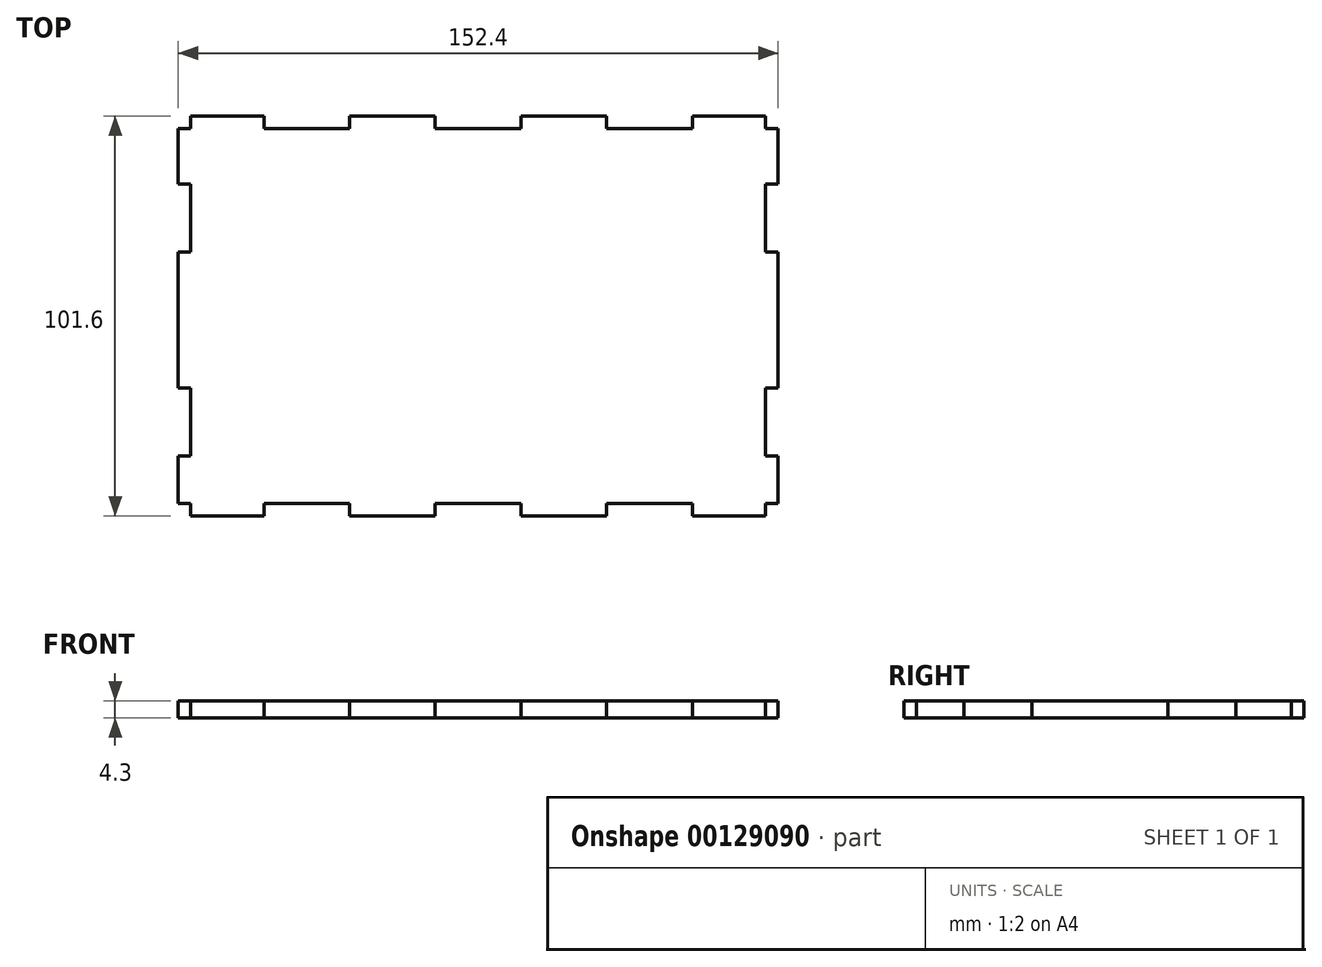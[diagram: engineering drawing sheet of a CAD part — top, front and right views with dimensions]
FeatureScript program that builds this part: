
annotation { "Feature Type Name" : "Feature", "Feature Type Description" : "" }
export const myFeature = defineFeature(function(context is Context, id is Id, definition is map)
    precondition{}
    {
        {
            var Q0;
            Q0=qCreatedBy(makeId("Top.planeOp"),FACE);
            var sketch = newSketch(context, id + "F0", { "sketchPlane" : qUnion([Q0])});
            skLineSegment(sketch, "E0.bottom", {"start": v(76.2, -50.8) * mm, "end": v(-76.2, -50.8) * mm});
            skLineSegment(sketch, "E0.top", {"start": v(76.2, 50.8) * mm, "end": v(-76.2, 50.8) * mm});
            skLineSegment(sketch, "E0.left", {"start": v(76.2, -50.8) * mm, "end": v(76.2, 50.8) * mm});
            skLineSegment(sketch, "E0.right", {"start": v(-76.2, -50.8) * mm, "end": v(-76.2, 50.8) * mm});
            skPoint(sketch, "E0.middle", {"position": v(0, 0) * mm});
            skLineSegment(sketch, "E1", {"start": v(-76.2, 50.8) * mm, "end": v(-73.03, 50.8) * mm});
            skLineSegment(sketch, "E2.0.1.0", {"start": v(-76.2, 33.53) * mm, "end": v(-73.03, 33.53) * mm});
            skLineSegment(sketch, "E2.0.2.0", {"start": v(-76.2, 16.27) * mm, "end": v(-73.03, 16.27) * mm});
            skLineSegment(sketch, "E2.0.3.0", {"start": v(-76.2, -1) * mm, "end": v(-73.03, -1) * mm});
            skLineSegment(sketch, "E2.0.4.0", {"start": v(-76.2, -18.27) * mm, "end": v(-73.03, -18.27) * mm});
            skLineSegment(sketch, "E2.0.5.0", {"start": v(-76.2, -35.53) * mm, "end": v(-73.03, -35.53) * mm});
            skLineSegment(sketch, "E2.direction1", {"start": v(-76.2, 50.8) * mm, "end": v(-50.8, 50.8) * mm, "construction": true});
            skLineSegment(sketch, "E2.direction2", {"start": v(-76.2, 50.8) * mm, "end": v(-76.2, 33.53) * mm, "construction": true});
            skLineSegment(sketch, "E3", {"start": v(-73.03, 50.8) * mm, "end": v(-73.02, -50.8) * mm});
            skLineSegment(sketch, "E4", {"start": v(-76.2, 50.8) * mm, "end": v(-76.2, 47.63) * mm});
            skLineSegment(sketch, "E5.1.0.0", {"start": v(-54.43, 50.8) * mm, "end": v(-54.43, 47.63) * mm});
            skLineSegment(sketch, "E5.2.0.0", {"start": v(-32.66, 50.8) * mm, "end": v(-32.66, 47.63) * mm});
            skLineSegment(sketch, "E5.3.0.0", {"start": v(-10.89, 50.8) * mm, "end": v(-10.89, 47.63) * mm});
            skLineSegment(sketch, "E5.4.0.0", {"start": v(10.89, 50.8) * mm, "end": v(10.89, 47.63) * mm});
            skLineSegment(sketch, "E5.5.0.0", {"start": v(32.66, 50.8) * mm, "end": v(32.66, 47.63) * mm});
            skLineSegment(sketch, "E5.6.0.0", {"start": v(54.43, 50.8) * mm, "end": v(54.43, 47.63) * mm});
            skLineSegment(sketch, "E5.7.0.0", {"start": v(76.2, 50.8) * mm, "end": v(76.2, 47.63) * mm});
            skLineSegment(sketch, "E5.direction1", {"start": v(-76.2, 47.63) * mm, "end": v(-54.43, 47.63) * mm, "construction": true});
            skLineSegment(sketch, "E6", {"start": v(-76.2, 47.63) * mm, "end": v(76.2, 47.63) * mm});
            skLineSegment(sketch, "E7.MirrorCS", {"start": v(76.2, 50.8) * mm, "end": v(73.03, 50.8) * mm});
            skLineSegment(sketch, "E8.MirrorCS", {"start": v(76.2, 33.53) * mm, "end": v(73.03, 33.53) * mm});
            skLineSegment(sketch, "E9.MirrorCS", {"start": v(76.2, 16.27) * mm, "end": v(73.03, 16.27) * mm});
            skLineSegment(sketch, "E10.MirrorCS", {"start": v(76.2, -1) * mm, "end": v(73.03, -1) * mm});
            skLineSegment(sketch, "E11.MirrorCS", {"start": v(76.2, -18.27) * mm, "end": v(73.03, -18.27) * mm});
            skLineSegment(sketch, "E12.MirrorCS", {"start": v(76.2, -35.53) * mm, "end": v(73.03, -35.53) * mm});
            skLineSegment(sketch, "E13.MirrorCS", {"start": v(76.2, 50.8) * mm, "end": v(76.2, 33.53) * mm, "construction": true});
            skLineSegment(sketch, "E14.MirrorCS", {"start": v(73.03, 50.8) * mm, "end": v(73.02, -50.8) * mm});
            skLineSegment(sketch, "E15.MirrorCS", {"start": v(76.2, -50.8) * mm, "end": v(76.2, -47.63) * mm});
            skLineSegment(sketch, "E16.MirrorCS", {"start": v(76.2, -50.8) * mm, "end": v(73.03, -50.8) * mm});
            skLineSegment(sketch, "E17.MirrorCS", {"start": v(-76.2, -50.8) * mm, "end": v(-76.2, -47.63) * mm});
            skLineSegment(sketch, "E18.MirrorCS", {"start": v(-76.2, -50.8) * mm, "end": v(-73.03, -50.8) * mm});
            skLineSegment(sketch, "E19.MirrorCS", {"start": v(-54.43, -50.8) * mm, "end": v(-54.43, -47.63) * mm});
            skLineSegment(sketch, "E20.MirrorCS", {"start": v(32.66, -50.8) * mm, "end": v(32.66, -47.63) * mm});
            skLineSegment(sketch, "E21.MirrorCS", {"start": v(10.89, -50.8) * mm, "end": v(10.89, -47.63) * mm});
            skLineSegment(sketch, "E22.MirrorCS", {"start": v(-10.89, -50.8) * mm, "end": v(-10.89, -47.63) * mm});
            skLineSegment(sketch, "E23.MirrorCS", {"start": v(54.43, -50.8) * mm, "end": v(54.43, -47.63) * mm});
            skLineSegment(sketch, "E24.MirrorCS", {"start": v(-32.66, -50.8) * mm, "end": v(-32.66, -47.63) * mm});
            skLineSegment(sketch, "E25.MirrorCS", {"start": v(-76.2, -47.63) * mm, "end": v(76.2, -47.63) * mm});
            skLineSegment(sketch, "E26.MirrorCS", {"start": v(-76.2, -47.63) * mm, "end": v(-54.43, -47.63) * mm, "construction": true});
            skLineSegment(sketch, "E27.MirrorCS", {"start": v(-76.2, -50.8) * mm, "end": v(-50.8, -50.8) * mm, "construction": true});
            skSolve(sketch);
        }
        {
            var Q0;
            {var subQ5=sQuery(id+"F0.wireOp",EDGE,"E8.MirrorCS");Q0=makeQuery(id+"F0.imprint","IMPRINT",FACE,{"disambiguationData":[TD([[makeQuery(id+"F0.imprint","IMPRINT",EDGE,{"derivedFrom":subQ5}),-1.0]])]});}
            var Q1;
            {var subQ0=sQuery(id+"F0.wireOp",EDGE,"E9.MirrorCS");Q1=makeQuery(id+"F0.imprint","IMPRINT",FACE,{"disambiguationData":[TD([[makeQuery(id+"F0.imprint","IMPRINT",EDGE,{"derivedFrom":subQ0}),1.0]])]});}
            var Q2;
            {var subQ0=sQuery(id+"F0.wireOp",EDGE,"E10.MirrorCS");Q2=makeQuery(id+"F0.imprint","IMPRINT",FACE,{"disambiguationData":[TD([[makeQuery(id+"F0.imprint","IMPRINT",EDGE,{"derivedFrom":subQ0}),1.0]])]});}
            var Q3;
            {var subQ0=sQuery(id+"F0.wireOp",EDGE,"E12.MirrorCS");Q3=makeQuery(id+"F0.imprint","IMPRINT",FACE,{"disambiguationData":[TD([[makeQuery(id+"F0.imprint","IMPRINT",EDGE,{"derivedFrom":subQ0}),1.0]])]});}
            var Q4;
            {var subQ5=sQuery(id+"F0.wireOp",EDGE,"E23.MirrorCS");Q4=makeQuery(id+"F0.imprint","IMPRINT",FACE,{"disambiguationData":[TD([[makeQuery(id+"F0.imprint","IMPRINT",EDGE,{"derivedFrom":subQ5}),-1.0]])]});}
            var Q5;
            {var subQ0=sQuery(id+"F0.wireOp",EDGE,"E20.MirrorCS");Q5=makeQuery(id+"F0.imprint","IMPRINT",FACE,{"disambiguationData":[TD([[makeQuery(id+"F0.imprint","IMPRINT",EDGE,{"derivedFrom":subQ0}),1.0]])]});}
            var Q6;
            {var subQ0=sQuery(id+"F0.wireOp",EDGE,"E22.MirrorCS");Q6=makeQuery(id+"F0.imprint","IMPRINT",FACE,{"disambiguationData":[TD([[makeQuery(id+"F0.imprint","IMPRINT",EDGE,{"derivedFrom":subQ0}),1.0]])]});}
            var Q7;
            {var subQ5=sQuery(id+"F0.wireOp",EDGE,"E19.MirrorCS");Q7=makeQuery(id+"F0.imprint","IMPRINT",FACE,{"disambiguationData":[TD([[makeQuery(id+"F0.imprint","IMPRINT",EDGE,{"derivedFrom":subQ5}),1.0]])]});}
            var Q8;
            {var subQ3=sQuery(id+"F0.wireOp",EDGE,"E2.0.5.0");Q8=makeQuery(id+"F0.imprint","IMPRINT",FACE,{"disambiguationData":[TD([[makeQuery(id+"F0.imprint","IMPRINT",EDGE,{"derivedFrom":subQ3}),-1.0]])]});}
            var Q9;
            {var subQ0=sQuery(id+"F0.wireOp",EDGE,"E2.0.3.0");Q9=makeQuery(id+"F0.imprint","IMPRINT",FACE,{"disambiguationData":[TD([[makeQuery(id+"F0.imprint","IMPRINT",EDGE,{"derivedFrom":subQ0}),-1.0]])]});}
            var Q10;
            {var subQ0=sQuery(id+"F0.wireOp",EDGE,"E2.0.2.0");Q10=makeQuery(id+"F0.imprint","IMPRINT",FACE,{"disambiguationData":[TD([[makeQuery(id+"F0.imprint","IMPRINT",EDGE,{"derivedFrom":subQ0}),-1.0]])]});}
            var Q11;
            {var subQ3=sQuery(id+"F0.wireOp",EDGE,"E2.0.1.0");Q11=makeQuery(id+"F0.imprint","IMPRINT",FACE,{"disambiguationData":[TD([[makeQuery(id+"F0.imprint","IMPRINT",EDGE,{"derivedFrom":subQ3}),1.0]])]});}
            var Q12;
            {var subQ3=sQuery(id+"F0.wireOp",EDGE,"E5.1.0.0");Q12=makeQuery(id+"F0.imprint","IMPRINT",FACE,{"disambiguationData":[TD([[makeQuery(id+"F0.imprint","IMPRINT",EDGE,{"derivedFrom":subQ3}),-1.0]])]});}
            var Q13;
            {var subQ0=sQuery(id+"F0.wireOp",EDGE,"E5.2.0.0");Q13=makeQuery(id+"F0.imprint","IMPRINT",FACE,{"disambiguationData":[TD([[makeQuery(id+"F0.imprint","IMPRINT",EDGE,{"derivedFrom":subQ0}),1.0]])]});}
            var Q14;
            {var subQ0=sQuery(id+"F0.wireOp",EDGE,"E5.4.0.0");Q14=makeQuery(id+"F0.imprint","IMPRINT",FACE,{"disambiguationData":[TD([[makeQuery(id+"F0.imprint","IMPRINT",EDGE,{"derivedFrom":subQ0}),1.0]])]});}
            var Q15;
            {var subQ3=sQuery(id+"F0.wireOp",EDGE,"E5.6.0.0");Q15=makeQuery(id+"F0.imprint","IMPRINT",FACE,{"disambiguationData":[TD([[makeQuery(id+"F0.imprint","IMPRINT",EDGE,{"derivedFrom":subQ3}),1.0]])]});}
            var Q16;
            {var subQ17=sQuery(id+"F0.wireOp",EDGE,"E3");var subQ23=makeQuery(id+"F0.imprint","INTERSECT",VERTEX,{"derivedFrom":[sQuery(id+"F0.wireOp",EDGE,"E2.0.1.0"),subQ17]});Q16=makeQuery(id+"F0.imprint","IMPRINT",FACE,{"disambiguationData":[TD([[makeQuery(id+"F0.imprint","IMPRINT",EDGE,{"disambiguationData":[TD([[subQ23,1.0]])],"derivedFrom":subQ17}),1.0]])]});}
            var Q17;
            {var subQ5=sQuery(id+"F0.wireOp",EDGE,"E7.MirrorCS");Q17=makeQuery(id+"F0.imprint","IMPRINT",FACE,{"disambiguationData":[TD([[makeQuery(id+"F0.imprint","IMPRINT",EDGE,{"derivedFrom":subQ5}),1.0]])]});}
            var Q18;
            {var subQ5=sQuery(id+"F0.wireOp",EDGE,"E15.MirrorCS");Q18=makeQuery(id+"F0.imprint","IMPRINT",FACE,{"disambiguationData":[TD([[makeQuery(id+"F0.imprint","IMPRINT",EDGE,{"derivedFrom":subQ5}),1.0]])]});}
            var Q19;
            {var subQ5=sQuery(id+"F0.wireOp",EDGE,"E17.MirrorCS");Q19=makeQuery(id+"F0.imprint","IMPRINT",FACE,{"disambiguationData":[TD([[makeQuery(id+"F0.imprint","IMPRINT",EDGE,{"derivedFrom":subQ5}),-1.0]])]});}
            var Q20;
            {var subQ0=sQuery(id+"F0.wireOp",EDGE,"E1");Q20=makeQuery(id+"F0.imprint","IMPRINT",FACE,{"disambiguationData":[TD([[makeQuery(id+"F0.imprint","IMPRINT",EDGE,{"derivedFrom":subQ0}),-1.0]])]});}
            extrude(context, id + "F1", {"entities" : qUnion([Q0, Q1, Q2, Q3, Q4, Q5, Q6, Q7, Q8, Q9, Q10, Q11, Q12, Q13, Q14, Q15, Q16, Q17, Q18, Q19, Q20]), "oppositeDirection" : true, "depth" : 4.3 * mm});
        }
    });
